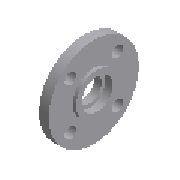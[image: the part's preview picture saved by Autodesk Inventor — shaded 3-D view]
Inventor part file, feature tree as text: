
AUTODESK INVENTOR PART (.ipt)
format: ipt  version: 2024.2 (Build 282272000, 272)  size: 205,312 bytes
history: native  units: mm (DEFAULTED — no unit token found)
features: other x5, revolve x1
ambient origin geometry x8: Origin, YZ Plane, XZ Plane, XY Plane, X Axis, Y Axis, Z Axis, Center Point
bodies: Solid1 (feature_tree)
feature tree (6):
  revolve  "Revolution1"  Angle=90.0deg
  other  "Work Axis1"
  other  "Work Point1"
  other  "Work Axis2"
  other  "Work Point2"
  other  "Work Point3"
